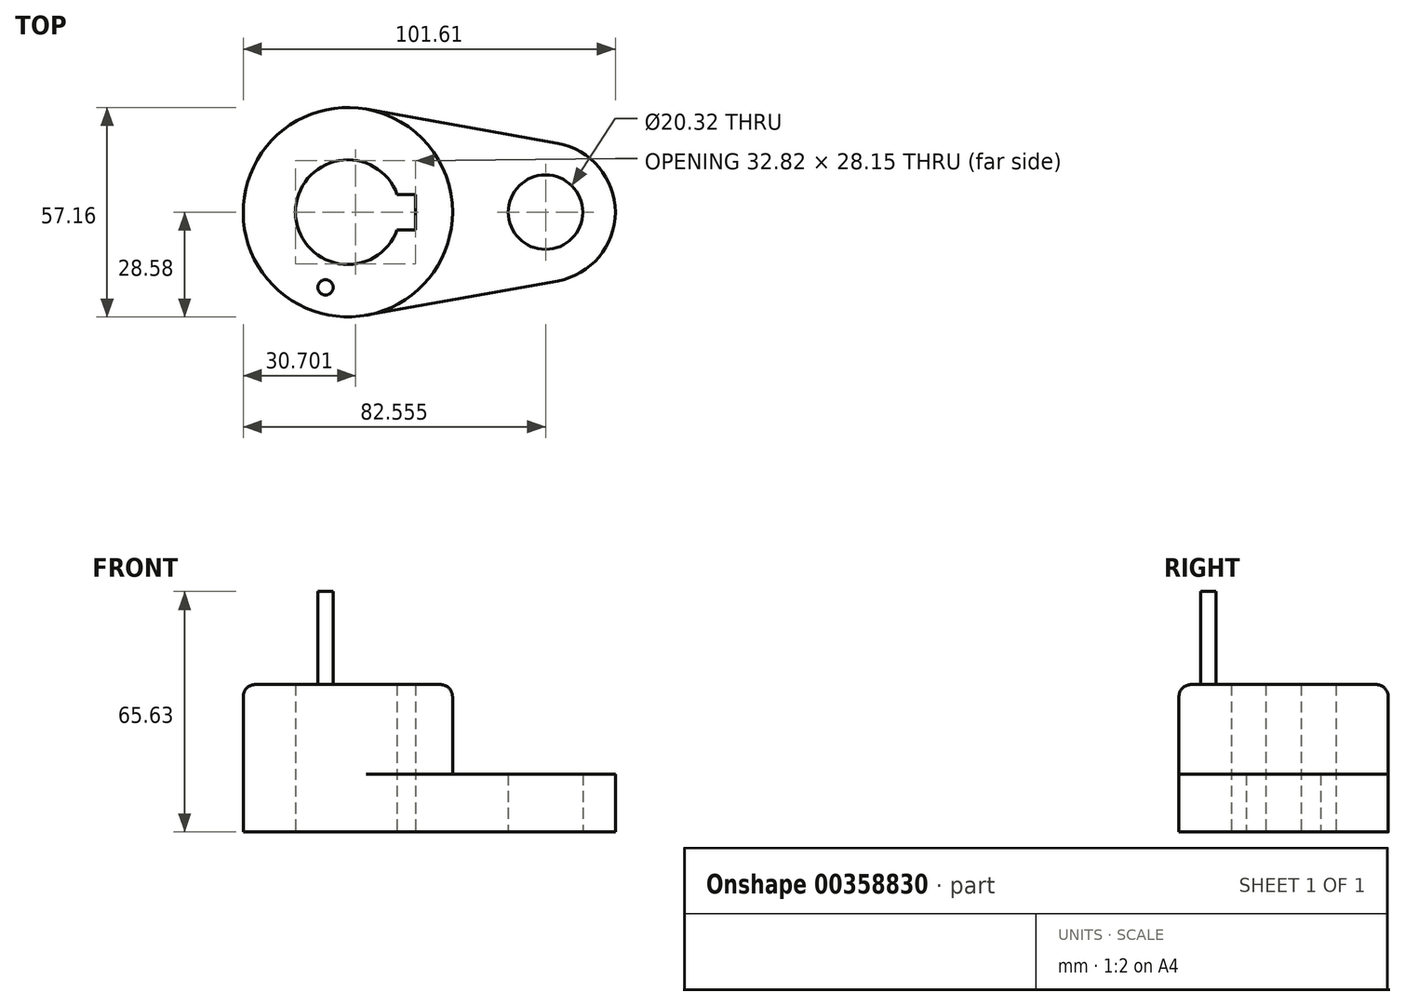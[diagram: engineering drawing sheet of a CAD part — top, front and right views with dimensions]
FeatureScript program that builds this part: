
annotation { "Feature Type Name" : "Feature", "Feature Type Description" : "" }
export const myFeature = defineFeature(function(context is Context, id is Id, definition is map)
    precondition{}
    {
        {
            var Q0;
            Q0=qCreatedBy(makeId("Top.planeOp"),FACE);
            var sketch = newSketch(context, id + "F0", { "sketchPlane" : qUnion([Q0])});
            skCircle(sketch, "E0", {"center": v(0, 0) * mm, "radius": 28.58 * mm});
            skArc(sketch, "E1", {"start": v(13.45, 4.83) * mm, "mid": v(-14.29, 0) * mm, "end": v(13.45, -4.83) * mm});
            skLineSegment(sketch, "E2", {"start": v(-39.33, 0) * mm, "end": v(67.23, 0) * mm, "construction": true});
            skLineSegment(sketch, "E3", {"start": v(13.45, 4.83) * mm, "end": v(18.53, 4.83) * mm});
            skLineSegment(sketch, "E4", {"start": v(18.53, 4.83) * mm, "end": v(18.53, -4.83) * mm});
            skLineSegment(sketch, "E5", {"start": v(18.53, -4.83) * mm, "end": v(13.45, -4.83) * mm});
            skSolve(sketch);
        }
        {
            var Q0;
            Q0 = qSketchRegion(id + "F0", true);
            extrude(context, id + "F1", {"entities" : qUnion([Q0]), "depth" : 40.23 * mm});
        }
        {
            var Q0;
            Q0=qCreatedBy(makeId("Top.planeOp"),FACE);
            var sketch = newSketch(context, id + "F2", { "sketchPlane" : qUnion([Q0])});
            skCircle(sketch, "E6", {"center": v(53.98, 0) * mm, "radius": 10.16 * mm});
            skArc(sketch, "E7", {"start": v(57.34, -18.75) * mm, "mid": v(73.03, 0) * mm, "end": v(57.34, 18.75) * mm});
            skArc(sketch, "E8", {"start": v(5.04, -28.13) * mm, "mid": v(28.58, 0) * mm, "end": v(5.04, 28.13) * mm});
            skLineSegment(sketch, "E9", {"start": v(57.34, -18.75) * mm, "end": v(5.04, -28.13) * mm});
            skLineSegment(sketch, "E10", {"start": v(57.34, 18.75) * mm, "end": v(5.04, 28.13) * mm});
            skSolve(sketch);
        }
        {
            var Q0;
            Q0=makeQuery(id+"F2.imprint","IMPRINT",FACE,{"disambiguationData":[TD([[makeQuery(id+"F2.imprint","IMPRINT",EDGE,{"derivedFrom":sQuery(id+"F2.wireOp",EDGE,"E6")}),-1.0]])]});
            extrude(context, id + "F3", {"entities" : qUnion([Q0]), "operationType" : NewBodyOperationType.ADD, "depth" : 15.77 * mm});
        }
        {
            var Q0;
            Q0=makeQuery(id+"F1.opExtrude","CAP_EDGE",EDGE,{"disambiguationData":[OSD([sQuery(id+"F0.wireOp",EDGE,"E0")])],"isStart":false});
            fillet(context, id + "F4", {"entities" : qUnion([Q0]), "radius" : 3.3 * mm, "tangentPropagation" : true, "allowEdgeOverflow" : false});
        }
        {
            var Q0;
            Q0=makeQuery(id+"F1.opExtrude","CAP_FACE",FACE,{"disambiguationData":[OSD([sQuery(id+"F0.wireOp",EDGE,"E0"),sQuery(id+"F0.wireOp",EDGE,"E1"),sQuery(id+"F0.wireOp",EDGE,"E3"),sQuery(id+"F0.wireOp",EDGE,"E4"),sQuery(id+"F0.wireOp",EDGE,"E5")])],"isStart":false});
            var sketch = newSketch(context, id + "F5", { "sketchPlane" : qUnion([Q0])});
            skCircle(sketch, "E11", {"center": v(-6.1, -20.53) * mm, "radius": 2.1 * mm});
            skSolve(sketch);
        }
        {
            var Q0;
            Q0 = qSketchRegion(id + "F5", true);
            extrude(context, id + "F6", {"entities" : qUnion([Q0]), "operationType" : NewBodyOperationType.ADD, "depth" : 25.4 * mm, "offsetDistance" : 25.4 * mm});
        }
    });
